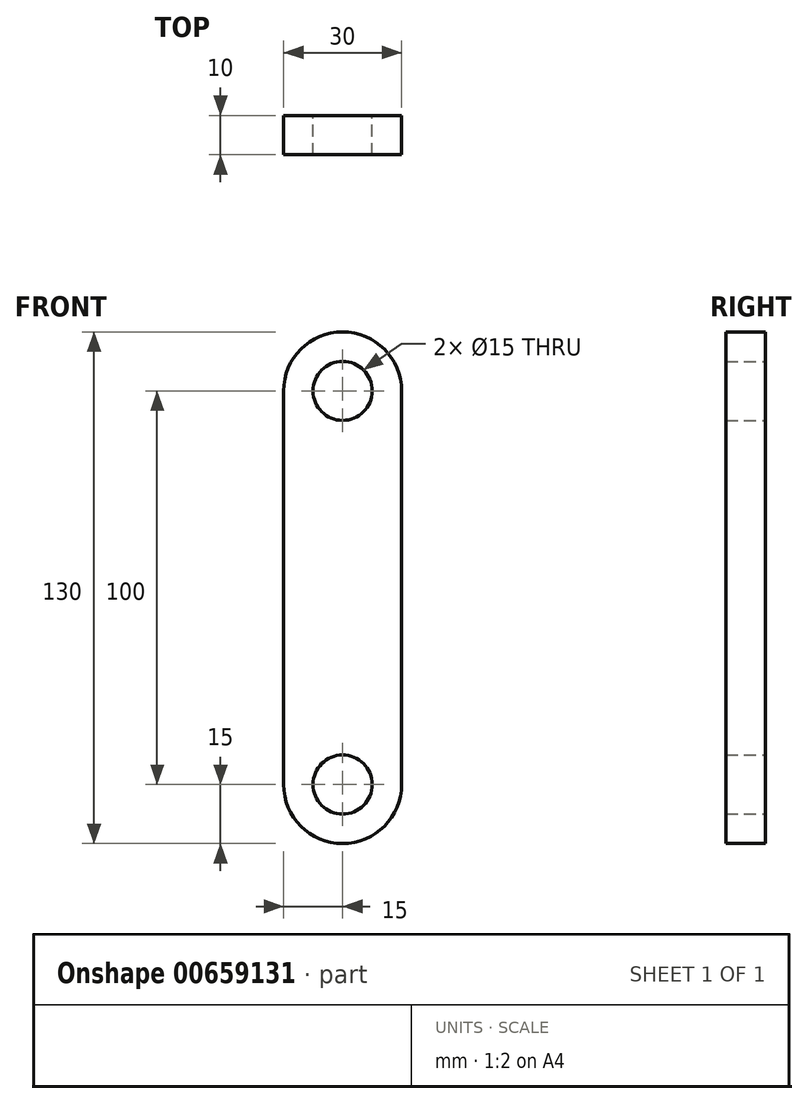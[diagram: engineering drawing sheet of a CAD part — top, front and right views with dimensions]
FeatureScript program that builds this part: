
annotation { "Feature Type Name" : "Feature", "Feature Type Description" : "" }
export const myFeature = defineFeature(function(context is Context, id is Id, definition is map)
    precondition{}
    {
        {
            var Q0;
            Q0=qCreatedBy(makeId("Front.planeOp"),FACE);
            var sketch = newSketch(context, id + "F0", { "sketchPlane" : qUnion([Q0])});
            skLineSegment(sketch, "E0", {"start": v(0, 65) * mm, "end": v(0, 0) * mm, "construction": true});
            skLineSegment(sketch, "E1", {"start": v(-15, 0) * mm, "end": v(15, 0) * mm, "construction": true});
            skCircle(sketch, "E2", {"center": v(0, 50) * mm, "radius": 7.5 * mm});
            skArc(sketch, "E3", {"start": v(15, 50) * mm, "mid": v(0, 65) * mm, "end": v(-15, 50) * mm});
            skLineSegment(sketch, "E4", {"start": v(-15, 50) * mm, "end": v(-15, 0) * mm});
            skLineSegment(sketch, "E5", {"start": v(15, 50) * mm, "end": v(15, 0) * mm});
            skArc(sketch, "E6.MirrorCS", {"start": v(15, -50) * mm, "mid": v(0, -65) * mm, "end": v(-15, -50) * mm});
            skCircle(sketch, "E7.MirrorC", {"center": v(0, -50) * mm, "radius": 7.5 * mm});
            skLineSegment(sketch, "E8.MirrorCS", {"start": v(15, -50) * mm, "end": v(15, 0) * mm});
            skLineSegment(sketch, "E9.MirrorCS", {"start": v(-15, -50) * mm, "end": v(-15, 0) * mm});
            skSolve(sketch);
        }
        {
            var Q0;
            Q0=qSketchRegion(id+"F0",true);
            extrude(context, id + "F1", {"entities" : qUnion([Q0]), "depth" : 10 * mm, "offsetDistance" : 25 * mm});
        }
    });
